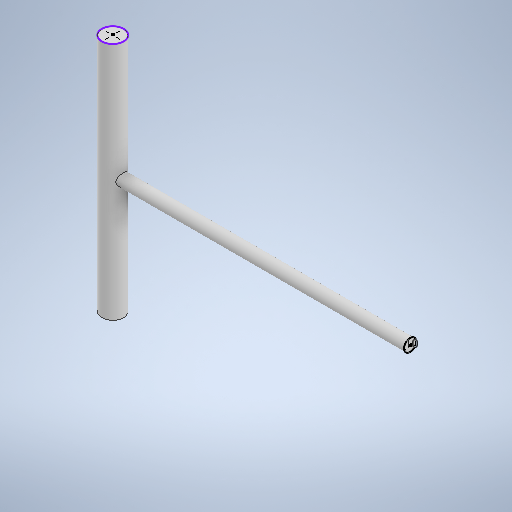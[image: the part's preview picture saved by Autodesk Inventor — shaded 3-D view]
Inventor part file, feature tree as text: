
AUTODESK INVENTOR PART (.ipt)
format: ipt  version: 2025.1 (Build 291241000, 241)  size: 261,632 bytes
history: native  units: mm
features: sketch x9, extrude x2, other x1
ambient origin geometry x8: Origin, YZ Plane, XZ Plane, XY Plane, X Axis, Y Axis, Z Axis, Center Point
bodies: Body1 (feature_tree)
feature tree (12):
  other  "ソリッド1"
  extrude  "押し出し1"  Depth=18.0mm
  sketch  "スケッチ2"
  sketch  "スケッチ3"
  sketch  "スケッチ4"
  extrude  "押し出し2"  Depth=99.0mm TaperAngle=0.0deg
  sketch  "スケッチ6"
  sketch  "スケッチ7"
  sketch  "スケッチ8"
  sketch  "スケッチ9"
  sketch  "スケッチ1"
  sketch  "スケッチ5"
